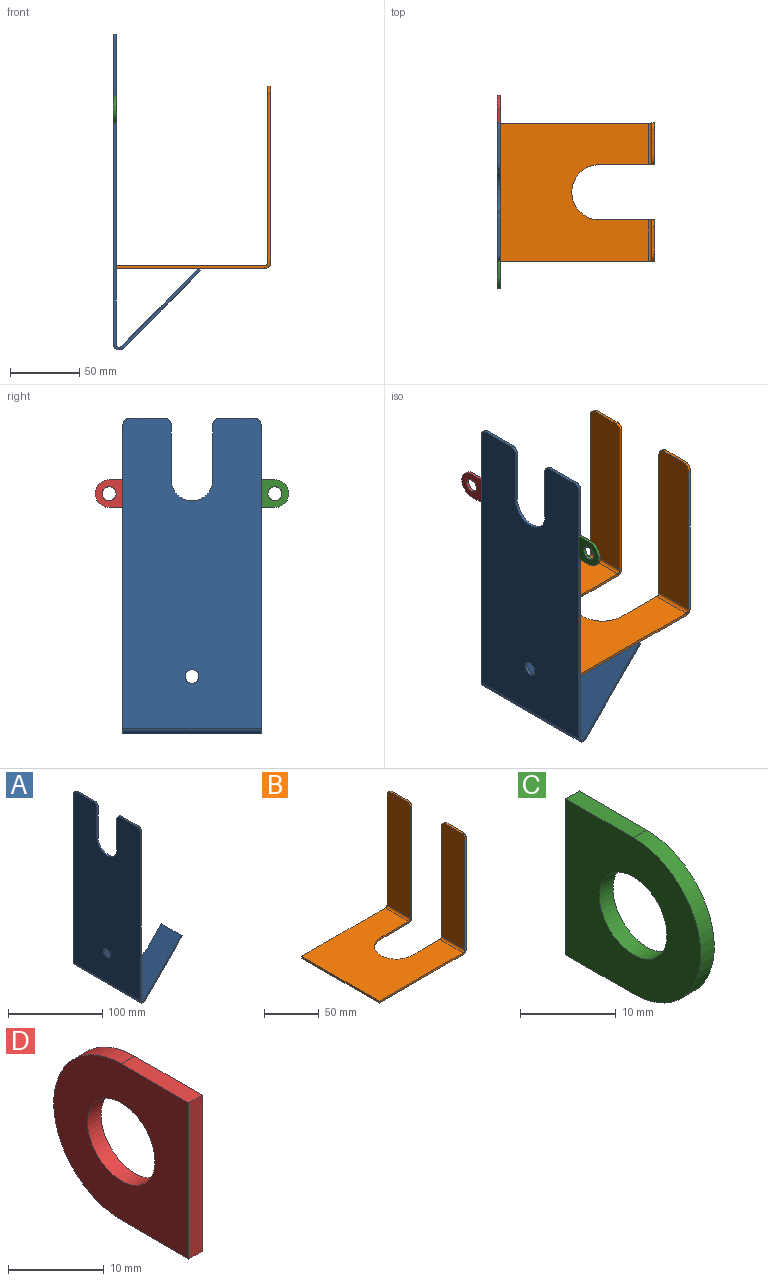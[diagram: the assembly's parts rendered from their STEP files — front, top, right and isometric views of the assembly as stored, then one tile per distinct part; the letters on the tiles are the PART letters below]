
ASSEMBLY  parts=4 mates=3
PART A: 27 faces, bbox 63.4x100x228.7 mm
  f0: cylinder r=15mm len=30mm, axis (-1,0,0), area 94.2mm2, adj f1,f7,f8,f9
  f1: plane 40x2mm, normal (0,-1,0), area 80mm2, adj f0,f8,f9,f12
  f2: plane 25x2mm, normal (0,0,1), area 50mm2, adj f8,f9,f11,f12
  f3: plane 219.45x2mm, normal (0,1,0), area 438.9mm2, adj f8,f9,f11,f24
  f4: plane 219.45x2mm, normal (0,-1,0), area 438.9mm2, adj f8,f9,f10,f23
  f5: plane 25x2mm, normal (0,0,1), area 50mm2, adj f8,f9,f10,f13
  f6: cylinder r=5mm len=10mm, axis (-1,0,0), area 62.8mm2, adj f8,f9
  f7: plane 40x2mm, normal (0,1,0), area 80mm2, adj f0,f8,f9,f13
  f8: plane 224.45x100mm, normal (-1,0,0), area 20641.3mm2, adj f0,f1,f2,f3,f4,f5,f6,f7
  f9: plane 224.45x100mm, normal (1,0,0), area 20641.3mm2, adj f0,f1,f2,f3,f4,f5,f6,f7
  f10: cylinder r=5mm len=5mm, axis (-1,0,0), area 15.7mm2, adj f4,f5,f8,f9
  f11: cylinder r=5mm len=5mm, axis (1,0,0), area 15.7mm2, adj f2,f3,f8,f9
  f12: cylinder r=5mm len=5mm, axis (1,0,0), area 15.7mm2, adj f1,f2,f8,f9
  f13: cylinder r=5mm len=5mm, axis (1,0,0), area 15.7mm2, adj f5,f7,f8,f9
  f14: extruded ~40x21.41mm, area 152.8mm2, adj f15,f20,f21,f22
  f15: plane 21.41x21.41mm, normal (0,1,0), area 56.6mm2, adj f14,f16,f21,f22
  f16: plane 30x1.41mm, normal (0.71,0,0.71), area 60mm2, adj f15,f17,f21,f22
  f17: plane 57.49x57.49mm, normal (0,-1,0), area 158.6mm2, adj f16,f21,f22,f23
  f18: plane 57.49x57.49mm, normal (0,1,0), area 158.6mm2, adj f19,f21,f22,f24
  f19: plane 30x1.41mm, normal (0.71,0,0.71), area 60mm2, adj f18,f20,f21,f22
  f20: plane 21.41x21.41mm, normal (0,-1,0), area 56.6mm2, adj f14,f19,f21,f22
  f21: plane 100x56.07mm, normal (0.71,0,-0.71), area 5910.1mm2, adj f14,f15,f16,f17,f18,f19,f20,f25
  f22: plane 100x56.07mm, normal (-0.71,0,0.71), area 5910.1mm2, adj f14,f15,f16,f17,f18,f19,f20,f26
  f23: plane 7.34x4.3mm, normal (0,-1,0), area 15.6mm2, adj f4,f17,f25,f26
  f24: plane 7.34x4.3mm, normal (0,1,0), area 15.6mm2, adj f3,f18,f25,f26
  f25: cylinder r=4.3mm len=100mm, axis (0,-1,0), area 1013.2mm2, adj f8,f21,f23,f24
  f26: cylinder r=2.3mm len=100mm, axis (0,-1,0), area 541.9mm2, adj f9,f22,f23,f24
PART B: 30 faces, bbox 112x100x132 mm
  f0: cylinder r=20mm len=40mm, axis (0,0,-1), area 125.7mm2, adj f1,f5,f6,f7
  f1: plane 35.7x2mm, normal (0,1,0), area 71.4mm2, adj f0,f6,f7,f27
  f2: plane 107.7x2mm, normal (0,-1,0), area 215.4mm2, adj f3,f6,f7,f26
  f3: plane 100x2mm, normal (-1,0,0), area 200mm2, adj f2,f4,f6,f7
  f4: plane 107.7x2mm, normal (0,1,0), area 215.4mm2, adj f3,f6,f7,f16
  f5: plane 35.7x2mm, normal (0,-1,0), area 71.4mm2, adj f0,f6,f7,f15
  f6: plane 107.7x100mm, normal (0,0,-1), area 8713.7mm2, adj f0,f1,f2,f3,f4,f5,f17,f28
  f7: plane 107.7x100mm, normal (0,0,1), area 8713.7mm2, adj f0,f1,f2,f3,f4,f5,f18,f29
  f8: plane 122.7x2mm, normal (0,1,0), area 245.4mm2, adj f11,f12,f13,f16
  f9: plane 20x2mm, normal (0,0,1), area 40mm2, adj f11,f12,f13,f14
  f10: plane 122.7x2mm, normal (0,-1,0), area 245.4mm2, adj f11,f12,f14,f15
  f11: plane 127.7x30mm, normal (1,0,0), area 3820.3mm2, adj f8,f9,f10,f13,f14,f17
  f12: plane 127.7x30mm, normal (-1,0,0), area 3820.3mm2, adj f8,f9,f10,f13,f14,f18
  f13: cylinder r=5mm len=5mm, axis (1,0,0), area 15.7mm2, adj f8,f9,f11,f12
  f14: cylinder r=5mm len=5mm, axis (1,0,0), area 15.7mm2, adj f9,f10,f11,f12
  f15: plane 4.3x4.3mm, normal (0,-1,0), area 10.4mm2, adj f5,f10,f17,f18
  f16: plane 4.3x4.3mm, normal (0,1,0), area 10.4mm2, adj f4,f8,f17,f18
  f17: cylinder r=4.3mm len=30mm, axis (0,-1,0), area 202.6mm2, adj f6,f11,f15,f16
  f18: cylinder r=2.3mm len=30mm, axis (0,-1,0), area 108.4mm2, adj f7,f12,f15,f16
  f19: plane 20x2mm, normal (0,0,1), area 40mm2, adj f22,f23,f24,f25
  f20: plane 122.7x2mm, normal (0,-1,0), area 245.4mm2, adj f22,f23,f24,f26
  f21: plane 122.7x2mm, normal (0,1,0), area 245.4mm2, adj f22,f23,f25,f27
  f22: plane 127.7x30mm, normal (1,0,0), area 3820.3mm2, adj f19,f20,f21,f24,f25,f28
  f23: plane 127.7x30mm, normal (-1,0,0), area 3820.3mm2, adj f19,f20,f21,f24,f25,f29
  f24: cylinder r=5mm len=5mm, axis (-1,0,0), area 15.7mm2, adj f19,f20,f22,f23
  f25: cylinder r=5mm len=5mm, axis (1,0,0), area 15.7mm2, adj f19,f21,f22,f23
  f26: plane 4.3x4.3mm, normal (0,-1,0), area 10.4mm2, adj f2,f20,f28,f29
  f27: plane 4.3x4.3mm, normal (0,1,0), area 10.4mm2, adj f1,f21,f28,f29
  f28: cylinder r=4.3mm len=30mm, axis (0,-1,0), area 202.6mm2, adj f6,f22,f26,f27
  f29: cylinder r=2.3mm len=30mm, axis (0,-1,0), area 108.4mm2, adj f7,f23,f26,f27
PART C: 7 faces, bbox 2x20x20 mm
  f0: plane 20x2mm, normal (0,1,0), area 40mm2, adj f1,f4,f5,f6
  f1: plane 10x2mm, normal (0,0,1), area 20mm2, adj f0,f2,f5,f6
  f2: cylinder r=10mm len=20mm, axis (1,0,0), area 62.8mm2, adj f1,f4,f5,f6
  f3: cylinder r=5mm len=10mm, axis (1,0,0), area 62.8mm2, adj f5,f6
  f4: plane 10x2mm, normal (0,0,-1), area 20mm2, adj f0,f2,f5,f6
  f5: plane 20x20mm, normal (-1,0,0), area 278.5mm2, adj f0,f1,f2,f3,f4
  f6: plane 20x20mm, normal (1,0,0), area 278.5mm2, adj f0,f1,f2,f3,f4
PART D: 7 faces, bbox 2x20x20 mm
  f0: plane 10x2mm, normal (0,0,1), area 20mm2, adj f1,f3,f5,f6
  f1: plane 20x2mm, normal (0,-1,0), area 40mm2, adj f0,f2,f5,f6
  f2: plane 10x2mm, normal (0,0,-1), area 20mm2, adj f1,f3,f5,f6
  f3: cylinder r=10mm len=20mm, axis (1,0,0), area 62.8mm2, adj f0,f2,f5,f6
  f4: cylinder r=5mm len=10mm, axis (1,0,0), area 62.8mm2, adj f5,f6
  f5: plane 20x20mm, normal (-1,0,0), area 278.5mm2, adj f0,f1,f2,f3,f4
  f6: plane 20x20mm, normal (1,0,0), area 278.5mm2, adj f0,f1,f2,f3,f4
PLACE A t=(5.6,49.65,-25.87)mm
PLACE B t=(5.56,49.65,-23.68)mm
PLACE C t=(5.6,29.65,-15.6)mm
PLACE D t=(5.6,49.65,-15.58)mm
MATE fastened C.f0 <-> A.f4  axis (0,1,0) through (-27.81,-50.35,60.46)mm
MATE fastened D.f1 <-> A.f3  axis (0,-1,0) through (-27.81,49.65,60.46)mm
MATE fastened B.f3 <-> A.f9  axis (-1,0,0) through (-26.81,-0.35,-53.56)mm
